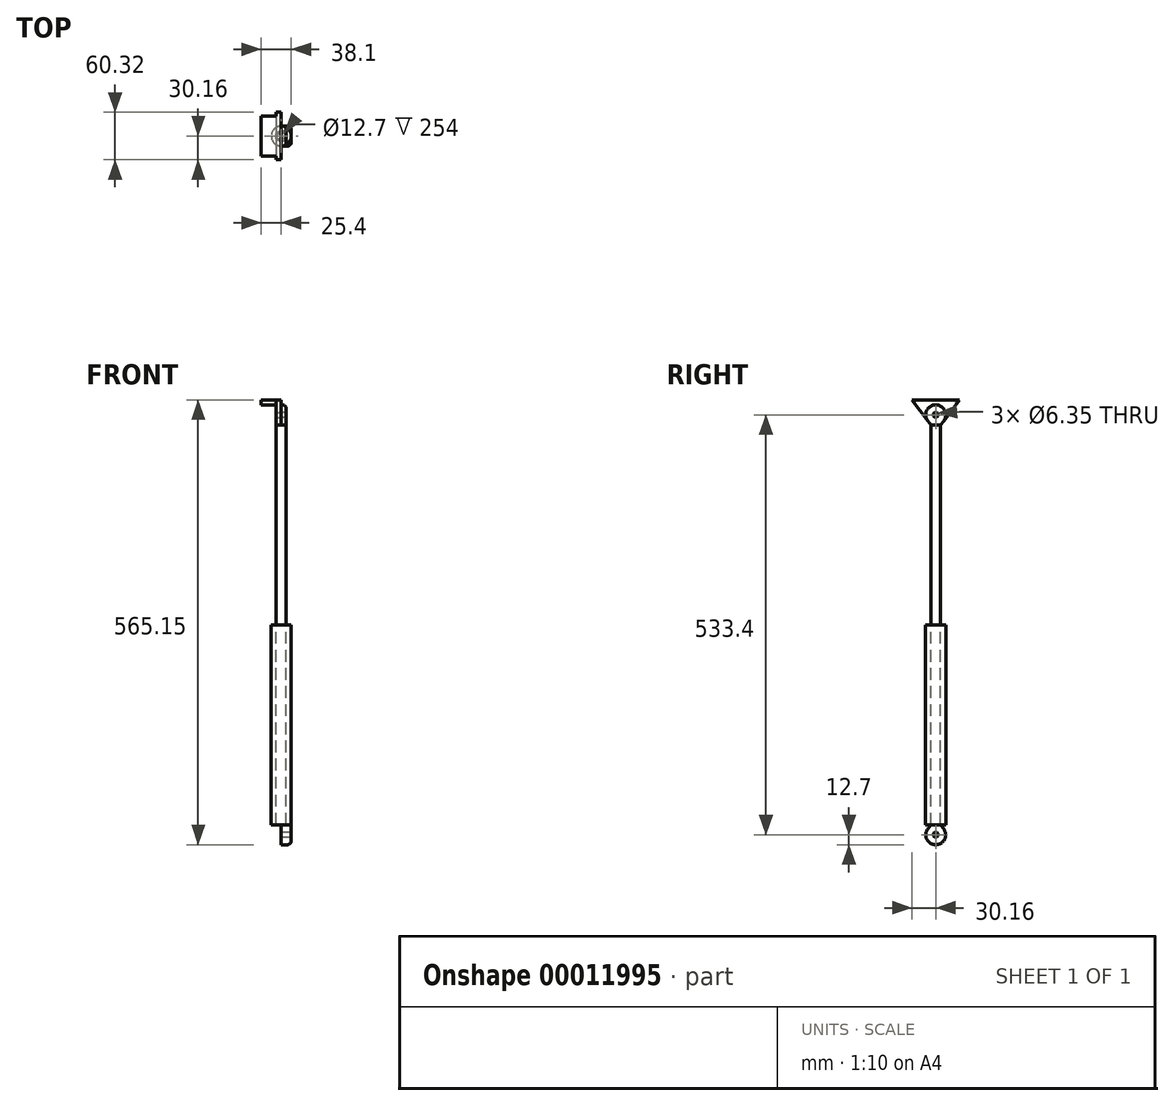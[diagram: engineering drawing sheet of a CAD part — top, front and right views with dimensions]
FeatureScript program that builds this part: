
annotation { "Feature Type Name" : "Feature", "Feature Type Description" : "" }
export const myFeature = defineFeature(function(context is Context, id is Id, definition is map)
    precondition{}
    {
        {
            var Q0;
            Q0=qCreatedBy(makeId("Top.planeOp"),FACE);
            var sketch = newSketch(context, id + "F0", { "sketchPlane" : qUnion([Q0])});
            skCircle(sketch, "E0", {"center": v(0, 0) * mm, "radius": 12.7 * mm});
            skCircle(sketch, "E1", {"center": v(0, 0) * mm, "radius": 6.35 * mm});
            skSolve(sketch);
        }
        {
            var Q0;
            Q0=makeQuery(id+"F0.imprint","IMPRINT",FACE,{"disambiguationData":[TD([[makeQuery(id+"F0.imprint","IMPRINT",EDGE,{"derivedFrom":sQuery(id+"F0.wireOp",EDGE,"E1")}),1.0]])]});
            extrude(context, id + "F1", {"entities" : qUnion([Q0]), "depth" : 254 * mm});
        }
        {
            var Q0;
            Q0=makeQuery(id+"F0.imprint","IMPRINT",FACE,{"disambiguationData":[TD([[makeQuery(id+"F0.imprint","IMPRINT",EDGE,{"derivedFrom":sQuery(id+"F0.wireOp",EDGE,"E0")}),1.0]])]});
            extrude(context, id + "F2", {"entities" : qUnion([Q0]), "operationType" : NewBodyOperationType.ADD, "oppositeDirection" : true, "depth" : 254 * mm});
        }
        {
            var Q0;
            Q0=qCreatedBy(makeId("Right.planeOp"),FACE);
            var sketch = newSketch(context, id + "F3", { "sketchPlane" : qUnion([Q0])});
            skCircle(sketch, "E2", {"center": v(0, 266.7) * mm, "radius": 3.18 * mm});
            skArc(sketch, "E3", {"start": v(10.16, 259.08) * mm, "mid": v(0, 279.4) * mm, "end": v(-10.16, 259.08) * mm});
            skLineSegment(sketch, "E4.0", {"start": v(-6.35, 254) * mm, "end": v(6.35, 254) * mm});
            skLineSegment(sketch, "E5", {"start": v(6.35, 254) * mm, "end": v(10.16, 259.08) * mm});
            skLineSegment(sketch, "E6", {"start": v(-6.35, 254) * mm, "end": v(-10.16, 259.08) * mm});
            skSolve(sketch);
        }
        {
            var Q0;
            Q0=makeQuery(id+"F3.imprint","IMPRINT",FACE,{"disambiguationData":[TD([[makeQuery(id+"F3.imprint","IMPRINT",EDGE,{"derivedFrom":sQuery(id+"F3.wireOp",EDGE,"E2")}),-1.0]])]});
            extrude(context, id + "F4", {"entities" : qUnion([Q0]), "operationType" : NewBodyOperationType.ADD, "depth" : 6.35 * mm});
        }
        {
            var Q0;
            Q0=makeQuery(id+"F4.opExtrude","CAP_EDGE",EDGE,{"disambiguationData":[OSD([sQuery(id+"F3.wireOp",EDGE,"E3")])],"isStart":false});
            var Q1;
            Q1=makeQuery(id+"F4.opExtrude","CAP_EDGE",EDGE,{"disambiguationData":[OSD([sQuery(id+"F3.wireOp",EDGE,"E5")])],"isStart":false});
            fillet(context, id + "F5", {"entities" : qUnion([Q0, Q1]), "radius" : 5.08 * mm, "tangentPropagation" : true, "allowEdgeOverflow" : false});
        }
        {
            var Q0;
            Q0=qCreatedBy(makeId("Right.planeOp"),FACE);
            var sketch = newSketch(context, id + "F6", { "sketchPlane" : qUnion([Q0])});
            skCircle(sketch, "E7", {"center": v(0, -266.7) * mm, "radius": 3.18 * mm});
            skArc(sketch, "E8", {"start": v(-10.16, -259.08) * mm, "mid": v(0, -279.4) * mm, "end": v(10.16, -259.08) * mm});
            skLineSegment(sketch, "E9", {"start": v(-6.35, -254) * mm, "end": v(-10.16, -259.08) * mm});
            skLineSegment(sketch, "E10", {"start": v(6.35, -254) * mm, "end": v(10.16, -259.08) * mm});
            skLineSegment(sketch, "E11.0", {"start": v(-6.35, -254) * mm, "end": v(6.35, -254) * mm});
            skPoint(sketch, "E12", {"position": v(0, -254) * mm});
            skSolve(sketch);
        }
        {
            var Q0;
            Q0=makeQuery(id+"F6.imprint","IMPRINT",FACE,{"disambiguationData":[TD([[makeQuery(id+"F6.imprint","IMPRINT",EDGE,{"derivedFrom":sQuery(id+"F6.wireOp",EDGE,"E7")}),-1.0]])]});
            extrude(context, id + "F7", {"entities" : qUnion([Q0]), "operationType" : NewBodyOperationType.ADD, "depth" : 12.7 * mm});
        }
        {
            var Q0;
            Q0=makeQuery(id+"F7.opExtrude","CAP_EDGE",EDGE,{"disambiguationData":[OSD([sQuery(id+"F6.wireOp",EDGE,"E8")])],"isStart":false});
            fillet(context, id + "F8", {"entities" : qUnion([Q0]), "radius" : 5.08 * mm, "tangentPropagation" : true, "allowEdgeOverflow" : false});
        }
        {
            var Q0;
            Q0=makeQuery(id+"F4.opExtrude","CAP_FACE",FACE,{"disambiguationData":[OSD([sQuery(id+"F3.wireOp",EDGE,"E2"),sQuery(id+"F3.wireOp",EDGE,"E3"),sQuery(id+"F3.wireOp",EDGE,"E4.0"),sQuery(id+"F3.wireOp",EDGE,"E5"),sQuery(id+"F3.wireOp",EDGE,"E6")])],"isStart":true});
            var sketch = newSketch(context, id + "F9", { "sketchPlane" : qUnion([Q0])});
            skArc(sketch, "E13.0", {"start": v(-10.16, 259.08) * mm, "mid": v(0, 279.4) * mm, "end": v(10.16, 259.08) * mm});
            skArc(sketch, "E14", {"start": v(-10.16, 259.08) * mm, "mid": v(0, 254) * mm, "end": v(10.16, 259.08) * mm});
            skLineSegment(sketch, "E15", {"start": v(10.16, 259.08) * mm, "end": v(30.16, 285.75) * mm});
            skLineSegment(sketch, "E16", {"start": v(30.16, 285.75) * mm, "end": v(-30.16, 285.75) * mm});
            skLineSegment(sketch, "E17", {"start": v(-30.16, 285.75) * mm, "end": v(-10.16, 259.08) * mm});
            skPoint(sketch, "E18", {"position": v(0, 285.75) * mm});
            skSolve(sketch);
        }
        {
            var Q0;
            Q0=makeQuery(id+"F9.imprint","IMPRINT",FACE,{"disambiguationData":[TD([[makeQuery(id+"F9.imprint","IMPRINT",EDGE,{"derivedFrom":sQuery(id+"F9.wireOp",EDGE,"E13.0")}),1.0]])]});
            var Q1;
            {var subQ2=sQuery(id+"F9.wireOp",EDGE,"E13.0");Q1=makeQuery(id+"F9.imprint","IMPRINT",FACE,{"disambiguationData":[TD([[makeQuery(id+"F9.imprint","IMPRINT",EDGE,{"derivedFrom":subQ2}),-1.0]])]});}
            extrude(context, id + "F10", {"entities" : qUnion([Q0, Q1]), "depth" : 6.35 * mm});
        }
        {
            var Q0;
            Q0=makeQuery(id+"F10.opExtrude","CAP_FACE",FACE,{"disambiguationData":[OSD([sQuery(id+"F3.wireOp",EDGE,"E2"),sQuery(id+"F9.wireOp",EDGE,"E14"),sQuery(id+"F9.wireOp",EDGE,"E15"),sQuery(id+"F9.wireOp",EDGE,"E16"),sQuery(id+"F9.wireOp",EDGE,"E17")])],"isStart":false});
            var sketch = newSketch(context, id + "F11", { "sketchPlane" : qUnion([Q0])});
            skLineSegment(sketch, "E19.0", {"start": v(30.16, 285.75) * mm, "end": v(-30.16, 285.75) * mm});
            skLineSegment(sketch, "E20.0", {"start": v(-30.16, 285.75) * mm, "end": v(-25.4, 279.4) * mm});
            skLineSegment(sketch, "E21.0", {"start": v(25.4, 279.4) * mm, "end": v(30.16, 285.75) * mm});
            skLineSegment(sketch, "E22", {"start": v(-25.4, 279.4) * mm, "end": v(25.4, 279.4) * mm});
            skPoint(sketch, "E23.orphan", {"position": v(-10.16, 259.08) * mm});
            skPoint(sketch, "E24.orphan", {"position": v(10.16, 259.08) * mm});
            skLineSegment(sketch, "E25", {"start": v(25.4, 279.4) * mm, "end": v(25.4, 285.75) * mm});
            skLineSegment(sketch, "E26", {"start": v(-25.4, 279.4) * mm, "end": v(-25.4, 285.75) * mm});
            skSolve(sketch);
        }
        {
            var Q0;
            Q0=makeQuery(id+"F11.imprint","IMPRINT",FACE,{"disambiguationData":[TD([[makeQuery(id+"F11.imprint","IMPRINT",EDGE,{"derivedFrom":sQuery(id+"F11.wireOp",EDGE,"E22")}),1.0]])]});
            extrude(context, id + "F12", {"entities" : qUnion([Q0]), "operationType" : NewBodyOperationType.ADD, "depth" : 19.05 * mm});
        }
    });
